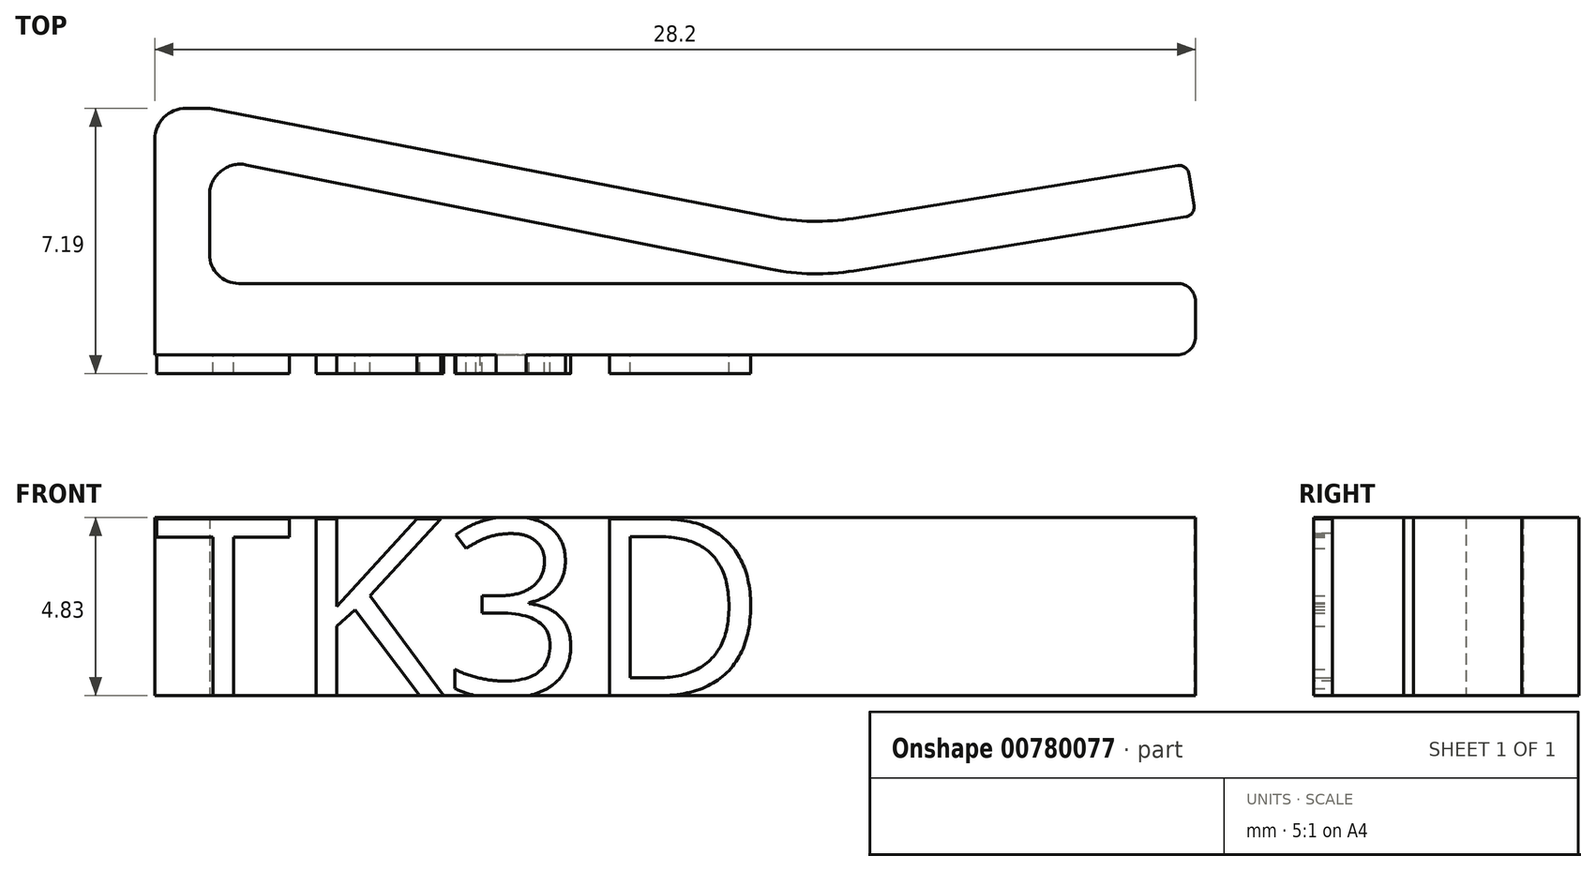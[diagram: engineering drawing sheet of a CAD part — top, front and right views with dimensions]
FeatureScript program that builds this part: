
annotation { "Feature Type Name" : "Feature", "Feature Type Description" : "" }
export const myFeature = defineFeature(function(context is Context, id is Id, definition is map)
    precondition{}
    {
        {
            var Q0;
            Q0=qCreatedBy(makeId("Top.planeOp"),FACE);
            var sketch = newSketch(context, id + "F0", { "sketchPlane" : qUnion([Q0])});
            skLineSegment(sketch, "E0", {"start": v(3.76, 0) * mm, "end": v(3.76, 1.93) * mm});
            skLineSegment(sketch, "E1", {"start": v(3.76, 1.93) * mm, "end": v(31.96, 1.93) * mm});
            skLineSegment(sketch, "E2", {"start": v(31.96, 1.93) * mm, "end": v(31.96, 0) * mm});
            skLineSegment(sketch, "E3", {"start": v(31.96, 0) * mm, "end": v(3.76, 0) * mm});
            skLineSegment(sketch, "E4", {"start": v(3.76, 1.93) * mm, "end": v(3.76, 6.37) * mm});
            skLineSegment(sketch, "E5", {"start": v(5.24, 5.35) * mm, "end": v(5.24, 1.93) * mm});
            skLineSegment(sketch, "E6", {"start": v(5.24, 5.35) * mm, "end": v(20.44, 2.32) * mm});
            skLineSegment(sketch, "E7", {"start": v(22.7, 2.28) * mm, "end": v(31.7, 3.74) * mm});
            skLineSegment(sketch, "E8", {"start": v(31.92, 4.04) * mm, "end": v(31.78, 4.9) * mm});
            skLineSegment(sketch, "E9", {"start": v(31.47, 5.13) * mm, "end": v(22.69, 3.7) * mm});
            skLineSegment(sketch, "E10", {"start": v(20.46, 3.73) * mm, "end": v(5.24, 6.68) * mm});
            skLineSegment(sketch, "E11", {"start": v(5.24, 6.68) * mm, "end": v(3.76, 6.68) * mm});
            skLineSegment(sketch, "E12", {"start": v(3.76, 6.68) * mm, "end": v(3.76, 6.37) * mm});
            skPoint(sketch, "E13.visualSharp", {"position": v(21.57, 2.1) * mm});
            skArc(sketch, "E13.filletArc", {"start": v(20.44, 2.32) * mm, "mid": v(21.57, 2.2) * mm, "end": v(22.7, 2.28) * mm});
            skPoint(sketch, "E14.visualSharp", {"position": v(21.57, 3.52) * mm});
            skArc(sketch, "E14.filletArc", {"start": v(20.46, 3.73) * mm, "mid": v(21.57, 3.62) * mm, "end": v(22.69, 3.7) * mm});
            skPoint(sketch, "E15.visualSharp", {"position": v(31.73, 5.17) * mm});
            skArc(sketch, "E15.filletArc", {"start": v(31.78, 4.9) * mm, "mid": v(31.67, 5.08) * mm, "end": v(31.47, 5.13) * mm});
            skPoint(sketch, "E16.visualSharp", {"position": v(31.96, 3.78) * mm});
            skArc(sketch, "E16.filletArc", {"start": v(31.7, 3.74) * mm, "mid": v(31.87, 3.84) * mm, "end": v(31.92, 4.04) * mm});
            skPoint(sketch, "E17.end.orphan", {"position": v(5.24, 6.37) * mm});
            skSolve(sketch);
        }
        {
            var Q0;
            {var subQ3=sQuery(id+"F0.wireOp",EDGE,"E0");Q0=makeQuery(id+"F0.imprint","IMPRINT",FACE,{"disambiguationData":[TD([[makeQuery(id+"F0.imprint","IMPRINT",EDGE,{"derivedFrom":subQ3}),-1.0]])]});}
            var Q1;
            {var subQ0=sQuery(id+"F0.wireOp",EDGE,"E4");Q1=makeQuery(id+"F0.imprint","IMPRINT",FACE,{"disambiguationData":[TD([[makeQuery(id+"F0.imprint","IMPRINT",EDGE,{"derivedFrom":subQ0}),-1.0]])]});}
            extrude(context, id + "F1", {"entities" : qUnion([Q0, Q1]), "depth" : 4.83 * mm, "offsetDistance" : 25.4 * mm});
        }
        {
            var Q0;
            Q0=makeQuery(id+"F1.opExtrude","SWEPT_EDGE",EDGE,{"disambiguationData":[OSD([sQuery(id+"F0.wireOp",EDGE,"E11"),sQuery(id+"F0.wireOp",EDGE,"E12")])]});
            fillet(context, id + "F2", {"entities" : qUnion([Q0]), "radius" : 0.84 * mm, "tangentPropagation" : true, "allowEdgeOverflow" : false});
        }
        {
            var Q0;
            Q0=makeQuery(id+"F1.opExtrude","SWEPT_EDGE",EDGE,{"disambiguationData":[OSD([sQuery(id+"F0.wireOp",EDGE,"E5"),sQuery(id+"F0.wireOp",EDGE,"E6")])]});
            fillet(context, id + "F3", {"entities" : qUnion([Q0]), "radius" : 0.84 * mm, "tangentPropagation" : true, "allowEdgeOverflow" : false});
        }
        {
            var Q0;
            Q0=makeQuery(id+"F1.opExtrude","SWEPT_EDGE",EDGE,{"disambiguationData":[OSD([sQuery(id+"F0.wireOp",EDGE,"E1"),sQuery(id+"F0.wireOp",EDGE,"E2")])]});
            fillet(context, id + "F4", {"entities" : qUnion([Q0]), "radius" : 0.5 * mm, "tangentPropagation" : true, "allowEdgeOverflow" : false});
        }
        {
            var Q0;
            Q0=makeQuery(id+"F1.opExtrude","SWEPT_EDGE",EDGE,{"disambiguationData":[OSD([sQuery(id+"F0.wireOp",EDGE,"E1"),sQuery(id+"F0.wireOp",EDGE,"E5")])]});
            fillet(context, id + "F5", {"entities" : qUnion([Q0]), "radius" : 0.8 * mm, "tangentPropagation" : true, "allowEdgeOverflow" : false});
        }
        {
            var Q0;
            Q0=makeQuery(id+"F1.opExtrude","SWEPT_FACE",FACE,{"disambiguationData":[OSD([sQuery(id+"F0.wireOp",EDGE,"E3")])]});
            var sketch = newSketch(context, id + "F6", { "sketchPlane" : qUnion([Q0])});
            skText(sketch, "E18", { "text": "TK3D\n", "fontName": "OpenSans-Regular.ttf"});
            const initialGuessF6  = {"E18": [0.00376, 0, 1, 0, 0.00483]};
            skSetInitialGuess(sketch, initialGuessF6);
            skSolve(sketch);
        }
        {
            var Q0;
            Q0=makeQuery(id+"F6.imprint","IMPRINT",FACE,{"disambiguationData":[TD([[makeQuery(id+"F6.imprint","IMPRINT",EDGE,{"derivedFrom":sQuery(id+"F6.wireOp",EDGE,"E18.sketch_text.stroke-0")}),-1.0]])]});
            var Q1;
            Q1=makeQuery(id+"F6.imprint","IMPRINT",FACE,{"disambiguationData":[TD([[makeQuery(id+"F6.imprint","IMPRINT",EDGE,{"derivedFrom":sQuery(id+"F6.wireOp",EDGE,"E18.sketch_text.stroke-8")}),-1.0]])]});
            var Q2;
            Q2=makeQuery(id+"F6.imprint","IMPRINT",FACE,{"disambiguationData":[TD([[makeQuery(id+"F6.imprint","IMPRINT",EDGE,{"derivedFrom":sQuery(id+"F6.wireOp",EDGE,"E18.sketch_text.stroke-20")}),-1.0]])]});
            var Q3;
            Q3=makeQuery(id+"F6.imprint","IMPRINT",FACE,{"disambiguationData":[TD([[makeQuery(id+"F6.imprint","IMPRINT",EDGE,{"derivedFrom":sQuery(id+"F6.wireOp",EDGE,"E18.sketch_text.stroke-48")}),-1.0]])]});
            extrude(context, id + "F7", {"entities" : qUnion([Q0, Q1, Q2, Q3]), "operationType" : NewBodyOperationType.ADD, "depth" : 0.5 * mm, "offsetDistance" : 25.4 * mm});
        }
        {
            var Q0;
            Q0=makeQuery(id+"F1.opExtrude","SWEPT_EDGE",EDGE,{"disambiguationData":[OSD([sQuery(id+"F0.wireOp",EDGE,"E2"),sQuery(id+"F0.wireOp",EDGE,"E3")])]});
            fillet(context, id + "F8", {"entities" : qUnion([Q0]), "radius" : 0.5 * mm, "tangentPropagation" : true, "allowEdgeOverflow" : false});
        }
    });
